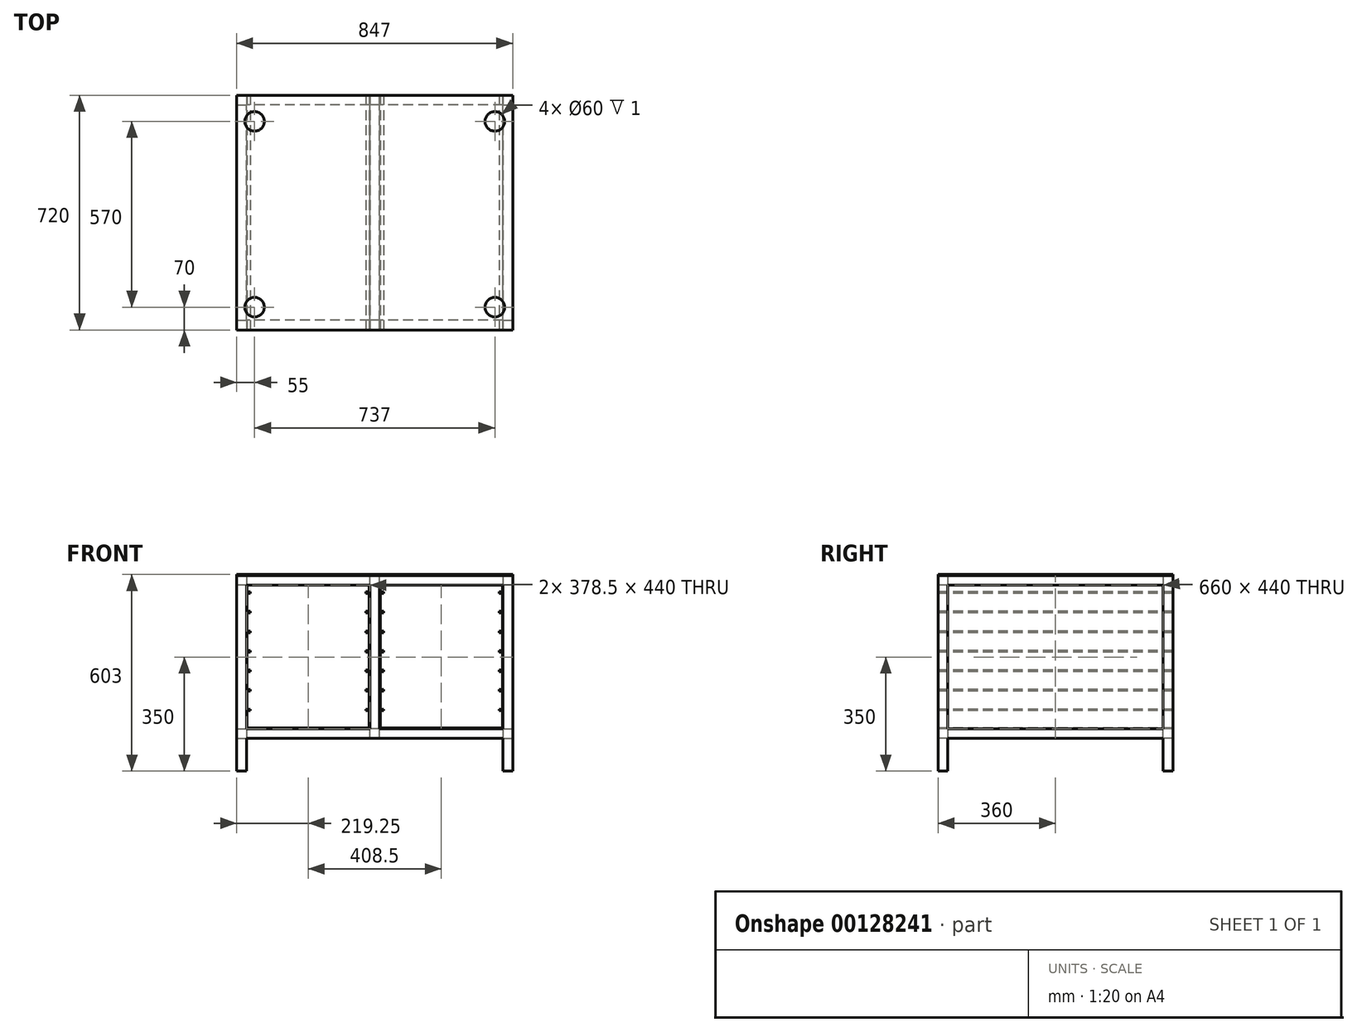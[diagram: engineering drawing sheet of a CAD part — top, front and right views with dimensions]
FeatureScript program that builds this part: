
annotation { "Feature Type Name" : "Feature", "Feature Type Description" : "" }
export const myFeature = defineFeature(function(context is Context, id is Id, definition is map)
    precondition{}
    {
        {
            var Q0;
            Q0=qCreatedBy(makeId("Top.planeOp"),FACE);
            var sketch = newSketch(context, id + "F0", { "sketchPlane" : qUnion([Q0])});
            skLineSegment(sketch, "E0.bottom", {"start": v(-423.5, 360) * mm, "end": v(-393.5, 360) * mm});
            skLineSegment(sketch, "E0.top", {"start": v(-423.5, 330) * mm, "end": v(-393.5, 330) * mm});
            skLineSegment(sketch, "E0.left", {"start": v(-423.5, 360) * mm, "end": v(-423.5, 330) * mm});
            skLineSegment(sketch, "E0.right", {"start": v(-393.5, 360) * mm, "end": v(-393.5, 330) * mm});
            skLineSegment(sketch, "E1.bottom", {"start": v(393.5, 360) * mm, "end": v(423.5, 360) * mm});
            skLineSegment(sketch, "E1.top", {"start": v(393.5, 330) * mm, "end": v(423.5, 330) * mm});
            skLineSegment(sketch, "E1.left", {"start": v(393.5, 360) * mm, "end": v(393.5, 330) * mm});
            skLineSegment(sketch, "E1.right", {"start": v(423.5, 360) * mm, "end": v(423.5, 330) * mm});
            skLineSegment(sketch, "E2.bottom", {"start": v(423.5, -330) * mm, "end": v(393.5, -330) * mm});
            skLineSegment(sketch, "E2.top", {"start": v(423.5, -360) * mm, "end": v(393.5, -360) * mm});
            skLineSegment(sketch, "E2.left", {"start": v(423.5, -330) * mm, "end": v(423.5, -360) * mm});
            skLineSegment(sketch, "E2.right", {"start": v(393.5, -330) * mm, "end": v(393.5, -360) * mm});
            skLineSegment(sketch, "E3.bottom", {"start": v(-423.5, -360) * mm, "end": v(-393.5, -360) * mm});
            skLineSegment(sketch, "E3.top", {"start": v(-423.5, -330) * mm, "end": v(-393.5, -330) * mm});
            skLineSegment(sketch, "E3.left", {"start": v(-423.5, -360) * mm, "end": v(-423.5, -330) * mm});
            skLineSegment(sketch, "E3.right", {"start": v(-393.5, -360) * mm, "end": v(-393.5, -330) * mm});
            skSolve(sketch);
        }
        {
            var Q0;
            Q0=makeQuery(id+"F0.imprint","IMPRINT",FACE,{"disambiguationData":[TD([[makeQuery(id+"F0.imprint","IMPRINT",EDGE,{"derivedFrom":sQuery(id+"F0.wireOp",EDGE,"E1.bottom")}),-1.0]])]});
            var Q1;
            Q1=makeQuery(id+"F0.imprint","IMPRINT",FACE,{"disambiguationData":[TD([[makeQuery(id+"F0.imprint","IMPRINT",EDGE,{"derivedFrom":sQuery(id+"F0.wireOp",EDGE,"E2.bottom")}),1.0]])]});
            var Q2;
            Q2=makeQuery(id+"F0.imprint","IMPRINT",FACE,{"disambiguationData":[TD([[makeQuery(id+"F0.imprint","IMPRINT",EDGE,{"derivedFrom":sQuery(id+"F0.wireOp",EDGE,"E0.bottom")}),-1.0]])]});
            var Q3;
            Q3=makeQuery(id+"F0.imprint","IMPRINT",FACE,{"disambiguationData":[TD([[makeQuery(id+"F0.imprint","IMPRINT",EDGE,{"derivedFrom":sQuery(id+"F0.wireOp",EDGE,"E3.bottom")}),1.0]])]});
            extrude(context, id + "F1", {"entities" : qUnion([Q0, Q1, Q2, Q3]), "depth" : 600 * mm});
        }
        {
            var Q0;
            Q0=qCreatedBy(makeId("Right.planeOp"),FACE);
            var sketch = newSketch(context, id + "F2", { "sketchPlane" : qUnion([Q0])});
            skLineSegment(sketch, "E4.bottom", {"start": v(360, 600) * mm, "end": v(330, 600) * mm});
            skLineSegment(sketch, "E4.top", {"start": v(360, 570) * mm, "end": v(330, 570) * mm});
            skLineSegment(sketch, "E4.left", {"start": v(360, 600) * mm, "end": v(360, 570) * mm});
            skLineSegment(sketch, "E4.right", {"start": v(330, 600) * mm, "end": v(330, 570) * mm});
            skLineSegment(sketch, "E5.bottom", {"start": v(-360, 600) * mm, "end": v(-330, 600) * mm});
            skLineSegment(sketch, "E5.top", {"start": v(-360, 570) * mm, "end": v(-330, 570) * mm});
            skLineSegment(sketch, "E5.left", {"start": v(-360, 600) * mm, "end": v(-360, 570) * mm});
            skLineSegment(sketch, "E5.right", {"start": v(-330, 600) * mm, "end": v(-330, 570) * mm});
            skLineSegment(sketch, "E6.bottom", {"start": v(360, 130) * mm, "end": v(330, 130) * mm});
            skLineSegment(sketch, "E6.top", {"start": v(360, 100) * mm, "end": v(330, 100) * mm});
            skLineSegment(sketch, "E6.left", {"start": v(360, 130) * mm, "end": v(360, 100) * mm});
            skLineSegment(sketch, "E6.right", {"start": v(330, 130) * mm, "end": v(330, 100) * mm});
            skLineSegment(sketch, "E7.bottom", {"start": v(-330, 130) * mm, "end": v(-360, 130) * mm});
            skLineSegment(sketch, "E7.top", {"start": v(-330, 100) * mm, "end": v(-360, 100) * mm});
            skLineSegment(sketch, "E7.left", {"start": v(-330, 130) * mm, "end": v(-330, 100) * mm});
            skLineSegment(sketch, "E7.right", {"start": v(-360, 130) * mm, "end": v(-360, 100) * mm});
            skSolve(sketch);
        }
        {
            var Q0;
            Q0 = qSketchRegion(id + "F2", true);
            extrude(context, id + "F3", {"entities" : qUnion([Q0]), "operationType" : NewBodyOperationType.ADD, "endBound" : BoundingType.UP_TO_NEXT, "depth" : 25 * mm, "hasSecondDirection" : true, "secondDirectionBound" : BoundingType.UP_TO_NEXT, "secondDirectionOppositeDirection" : true, "secondDirectionDepth" : 25 * mm});
        }
        {
            var Q0;
            Q0=qCreatedBy(makeId("Front.planeOp"),FACE);
            var sketch = newSketch(context, id + "F4", { "sketchPlane" : qUnion([Q0])});
            skLineSegment(sketch, "E8.bottom", {"start": v(423.5, 100) * mm, "end": v(393.5, 100) * mm});
            skLineSegment(sketch, "E8.top", {"start": v(423.5, 130) * mm, "end": v(393.5, 130) * mm});
            skLineSegment(sketch, "E8.left", {"start": v(423.5, 100) * mm, "end": v(423.5, 130) * mm});
            skLineSegment(sketch, "E8.right", {"start": v(393.5, 100) * mm, "end": v(393.5, 130) * mm});
            skPoint(sketch, "E9.oppositeSnap0", {"position": v(408.5, 130) * mm});
            skLineSegment(sketch, "E9.bottom", {"start": v(-393.5, 100) * mm, "end": v(-423.5, 100) * mm});
            skLineSegment(sketch, "E9.top", {"start": v(-393.5, 130) * mm, "end": v(-423.5, 130) * mm});
            skLineSegment(sketch, "E9.left", {"start": v(-393.5, 100) * mm, "end": v(-393.5, 130) * mm});
            skLineSegment(sketch, "E9.right", {"start": v(-423.5, 100) * mm, "end": v(-423.5, 130) * mm});
            skLineSegment(sketch, "E10.bottom", {"start": v(-423.5, 570) * mm, "end": v(-393.5, 570) * mm});
            skLineSegment(sketch, "E10.top", {"start": v(-423.5, 600) * mm, "end": v(-393.5, 600) * mm});
            skLineSegment(sketch, "E10.left", {"start": v(-423.5, 570) * mm, "end": v(-423.5, 600) * mm});
            skLineSegment(sketch, "E10.right", {"start": v(-393.5, 570) * mm, "end": v(-393.5, 600) * mm});
            skLineSegment(sketch, "E11.bottom", {"start": v(393.5, 570) * mm, "end": v(423.5, 570) * mm});
            skLineSegment(sketch, "E11.top", {"start": v(393.5, 600) * mm, "end": v(423.5, 600) * mm});
            skLineSegment(sketch, "E11.left", {"start": v(393.5, 570) * mm, "end": v(393.5, 600) * mm});
            skLineSegment(sketch, "E11.right", {"start": v(423.5, 570) * mm, "end": v(423.5, 600) * mm});
            skLineSegment(sketch, "E12.bottom", {"start": v(-15, 130) * mm, "end": v(15, 130) * mm});
            skLineSegment(sketch, "E12.top", {"start": v(-15, 100) * mm, "end": v(15, 100) * mm});
            skLineSegment(sketch, "E12.left", {"start": v(-15, 130) * mm, "end": v(-15, 100) * mm});
            skLineSegment(sketch, "E12.right", {"start": v(15, 130) * mm, "end": v(15, 100) * mm});
            skLineSegment(sketch, "E13.bottom", {"start": v(-15, 600) * mm, "end": v(15, 600) * mm});
            skLineSegment(sketch, "E13.top", {"start": v(-15, 570) * mm, "end": v(15, 570) * mm});
            skLineSegment(sketch, "E13.left", {"start": v(-15, 600) * mm, "end": v(-15, 570) * mm});
            skLineSegment(sketch, "E13.right", {"start": v(15, 600) * mm, "end": v(15, 570) * mm});
            skSolve(sketch);
        }
        {
            var Q0;
            Q0 = qSketchRegion(id + "F4", true);
            extrude(context, id + "F5", {"entities" : qUnion([Q0]), "operationType" : NewBodyOperationType.ADD, "endBound" : BoundingType.UP_TO_NEXT, "depth" : 25 * mm, "hasSecondDirection" : true, "secondDirectionBound" : BoundingType.UP_TO_NEXT, "secondDirectionOppositeDirection" : true, "secondDirectionDepth" : 25 * mm});
        }
        {
            var Q0;
            Q0=makeQuery(id+"F5.boolean.opBoolean","MERGE",FACE,{"derivedFrom":[makeQuery(id+"F3.boolean.opBoolean","MERGE",FACE,{"derivedFrom":[makeQuery(id+"F1.opExtrude","CAP_FACE",FACE,{"disambiguationData":[OSD([sQuery(id+"F0.wireOp",EDGE,"E0.bottom"),sQuery(id+"F0.wireOp",EDGE,"E0.top"),sQuery(id+"F0.wireOp",EDGE,"E0.left"),sQuery(id+"F0.wireOp",EDGE,"E0.right")])],"isStart":false}),makeQuery(id+"F1.opExtrude","CAP_FACE",FACE,{"disambiguationData":[OSD([sQuery(id+"F0.wireOp",EDGE,"E1.bottom"),sQuery(id+"F0.wireOp",EDGE,"E1.top"),sQuery(id+"F0.wireOp",EDGE,"E1.left"),sQuery(id+"F0.wireOp",EDGE,"E1.right")])],"isStart":false}),makeQuery(id+"F3.opExtrude","SWEPT_FACE",FACE,{"disambiguationData":[OSD([sQuery(id+"F2.wireOp",EDGE,"E4.bottom")])]})]}),makeQuery(id+"F3.boolean.opBoolean","MERGE",FACE,{"derivedFrom":[makeQuery(id+"F1.opExtrude","CAP_FACE",FACE,{"disambiguationData":[OSD([sQuery(id+"F0.wireOp",EDGE,"E2.bottom"),sQuery(id+"F0.wireOp",EDGE,"E2.top"),sQuery(id+"F0.wireOp",EDGE,"E2.left"),sQuery(id+"F0.wireOp",EDGE,"E2.right")])],"isStart":false}),makeQuery(id+"F1.opExtrude","CAP_FACE",FACE,{"disambiguationData":[OSD([sQuery(id+"F0.wireOp",EDGE,"E3.bottom"),sQuery(id+"F0.wireOp",EDGE,"E3.top"),sQuery(id+"F0.wireOp",EDGE,"E3.left"),sQuery(id+"F0.wireOp",EDGE,"E3.right")])],"isStart":false}),makeQuery(id+"F3.opExtrude","SWEPT_FACE",FACE,{"disambiguationData":[OSD([sQuery(id+"F2.wireOp",EDGE,"E5.bottom")])]})]}),makeQuery(id+"F5.opExtrude","SWEPT_FACE",FACE,{"disambiguationData":[OSD([sQuery(id+"F4.wireOp",EDGE,"E10.top")])]}),makeQuery(id+"F5.opExtrude","SWEPT_FACE",FACE,{"disambiguationData":[OSD([sQuery(id+"F4.wireOp",EDGE,"E11.top")])]})]});
            var sketch = newSketch(context, id + "F6", { "sketchPlane" : qUnion([Q0])});
            skLineSegment(sketch, "E14.bottom", {"start": v(-423.5, -360) * mm, "end": v(423.5, -360) * mm});
            skLineSegment(sketch, "E14.top", {"start": v(-423.5, 360) * mm, "end": v(423.5, 360) * mm});
            skLineSegment(sketch, "E14.left", {"start": v(-423.5, -360) * mm, "end": v(-423.5, 360) * mm});
            skLineSegment(sketch, "E14.right", {"start": v(423.5, -360) * mm, "end": v(423.5, 360) * mm});
            skSolve(sketch);
        }
        {
            var Q0;
            Q0 = qSketchRegion(id + "F6", true);
            extrude(context, id + "F7", {"entities" : qUnion([Q0]), "depth" : 3 * mm});
        }
        {
            var Q0;
            Q0=qCreatedBy(makeId("Top.planeOp"),FACE);
            cPlane(context, id + "F8", {"entities" : qUnion([Q0]), "cplaneType" : CPlaneType.OFFSET, "offset" : 300 * mm, "width" : 150 * mm, "height" : 150 * mm});
        }
        {
            var Q0;
            Q0=qCreatedBy(id+"F8.planeOp",FACE);
            var sketch = newSketch(context, id + "F9", { "sketchPlane" : qUnion([Q0])});
            skLineSegment(sketch, "E15.bottom", {"start": v(-15, 360) * mm, "end": v(15, 360) * mm});
            skLineSegment(sketch, "E15.top", {"start": v(-15, 330) * mm, "end": v(15, 330) * mm});
            skLineSegment(sketch, "E15.left", {"start": v(-15, 360) * mm, "end": v(-15, 330) * mm});
            skLineSegment(sketch, "E15.right", {"start": v(15, 360) * mm, "end": v(15, 330) * mm});
            skLineSegment(sketch, "E16.bottom", {"start": v(-15, -330) * mm, "end": v(15, -330) * mm});
            skLineSegment(sketch, "E16.top", {"start": v(-15, -360) * mm, "end": v(15, -360) * mm});
            skLineSegment(sketch, "E16.left", {"start": v(-15, -330) * mm, "end": v(-15, -360) * mm});
            skLineSegment(sketch, "E16.right", {"start": v(15, -330) * mm, "end": v(15, -360) * mm});
            skSolve(sketch);
        }
        {
            var Q0;
            Q0 = qSketchRegion(id + "F9", true);
            extrude(context, id + "F10", {"entities" : qUnion([Q0]), "operationType" : NewBodyOperationType.ADD, "endBound" : BoundingType.UP_TO_NEXT, "depth" : 25 * mm, "hasSecondDirection" : true, "secondDirectionBound" : BoundingType.UP_TO_NEXT, "secondDirectionOppositeDirection" : true, "secondDirectionDepth" : 25 * mm});
        }
        {
            var Q0;
            Q0=makeQuery(id+"F10.boolean.opBoolean","MERGE",FACE,{"derivedFrom":[makeQuery(id+"F3.boolean.opBoolean","MERGE",FACE,{"derivedFrom":[makeQuery(id+"F1.opExtrude","SWEPT_FACE",FACE,{"disambiguationData":[OSD([sQuery(id+"F0.wireOp",EDGE,"E2.top")])]}),makeQuery(id+"F1.opExtrude","SWEPT_FACE",FACE,{"disambiguationData":[OSD([sQuery(id+"F0.wireOp",EDGE,"E3.bottom")])]}),makeQuery(id+"F3.opExtrude","SWEPT_FACE",FACE,{"disambiguationData":[OSD([sQuery(id+"F2.wireOp",EDGE,"E5.left")])]}),makeQuery(id+"F3.opExtrude","SWEPT_FACE",FACE,{"disambiguationData":[OSD([sQuery(id+"F2.wireOp",EDGE,"E7.right")])]})]}),makeQuery(id+"F10.opExtrude","SWEPT_FACE",FACE,{"disambiguationData":[OSD([sQuery(id+"F9.wireOp",EDGE,"E16.top")])]})]});
            var sketch = newSketch(context, id + "F11", { "sketchPlane" : qUnion([Q0])});
            skLineSegment(sketch, "E17.bottom", {"start": v(-393.5, 570) * mm, "end": v(-391.5, 570) * mm});
            skLineSegment(sketch, "E17.top", {"start": v(-393.5, 130) * mm, "end": v(-391.5, 130) * mm});
            skLineSegment(sketch, "E17.left", {"start": v(-393.5, 570) * mm, "end": v(-393.5, 130) * mm});
            skLineSegment(sketch, "E17.right", {"start": v(-391.5, 570) * mm, "end": v(-391.5, 130) * mm});
            skLineSegment(sketch, "E18.bottom", {"start": v(-15, 570) * mm, "end": v(-17, 570) * mm});
            skLineSegment(sketch, "E18.top", {"start": v(-15, 130) * mm, "end": v(-17, 130) * mm});
            skLineSegment(sketch, "E18.left", {"start": v(-15, 570) * mm, "end": v(-15, 130) * mm});
            skLineSegment(sketch, "E18.right", {"start": v(-17, 570) * mm, "end": v(-17, 130) * mm});
            skLineSegment(sketch, "E19.bottom", {"start": v(15, 570) * mm, "end": v(17, 570) * mm});
            skLineSegment(sketch, "E19.top", {"start": v(15, 130) * mm, "end": v(17, 130) * mm});
            skLineSegment(sketch, "E19.left", {"start": v(15, 570) * mm, "end": v(15, 130) * mm});
            skLineSegment(sketch, "E19.right", {"start": v(17, 570) * mm, "end": v(17, 130) * mm});
            skLineSegment(sketch, "E20.bottom", {"start": v(393.5, 570) * mm, "end": v(391.5, 570) * mm});
            skLineSegment(sketch, "E20.top", {"start": v(393.5, 130) * mm, "end": v(391.5, 130) * mm});
            skLineSegment(sketch, "E20.left", {"start": v(393.5, 570) * mm, "end": v(393.5, 130) * mm});
            skLineSegment(sketch, "E20.right", {"start": v(391.5, 570) * mm, "end": v(391.5, 130) * mm});
            skLineSegment(sketch, "E21.bottom", {"start": v(-391.5, 130) * mm, "end": v(-17, 130) * mm});
            skLineSegment(sketch, "E21.top", {"start": v(-391.5, 132) * mm, "end": v(-17, 132) * mm});
            skLineSegment(sketch, "E21.left", {"start": v(-391.5, 130) * mm, "end": v(-391.5, 132) * mm});
            skLineSegment(sketch, "E21.right", {"start": v(-17, 130) * mm, "end": v(-17, 132) * mm});
            skLineSegment(sketch, "E22.bottom", {"start": v(17, 130) * mm, "end": v(391.5, 130) * mm});
            skLineSegment(sketch, "E22.top", {"start": v(17, 132) * mm, "end": v(391.5, 132) * mm});
            skLineSegment(sketch, "E22.left", {"start": v(17, 130) * mm, "end": v(17, 132) * mm});
            skLineSegment(sketch, "E22.right", {"start": v(391.5, 130) * mm, "end": v(391.5, 132) * mm});
            skSolve(sketch);
        }
        {
            var Q0;
            Q0 = qSketchRegion(id + "F11", true);
            extrude(context, id + "F12", {"entities" : qUnion([Q0]), "oppositeDirection" : true, "depth" : 720 * mm});
        }
        {
            var Q0;
            Q0=makeQuery(id+"F10.boolean.opBoolean","MERGE",FACE,{"derivedFrom":[makeQuery(id+"F3.boolean.opBoolean","MERGE",FACE,{"derivedFrom":[makeQuery(id+"F1.opExtrude","SWEPT_FACE",FACE,{"disambiguationData":[OSD([sQuery(id+"F0.wireOp",EDGE,"E2.top")])]}),makeQuery(id+"F1.opExtrude","SWEPT_FACE",FACE,{"disambiguationData":[OSD([sQuery(id+"F0.wireOp",EDGE,"E3.bottom")])]}),makeQuery(id+"F3.opExtrude","SWEPT_FACE",FACE,{"disambiguationData":[OSD([sQuery(id+"F2.wireOp",EDGE,"E5.left")])]}),makeQuery(id+"F3.opExtrude","SWEPT_FACE",FACE,{"disambiguationData":[OSD([sQuery(id+"F2.wireOp",EDGE,"E7.right")])]})]}),makeQuery(id+"F10.opExtrude","SWEPT_FACE",FACE,{"disambiguationData":[OSD([sQuery(id+"F9.wireOp",EDGE,"E16.top")])]})]});
            var sketch = newSketch(context, id + "F13", { "sketchPlane" : qUnion([Q0])});
            skLineSegment(sketch, "E23.bottom", {"start": v(-391.5, 550) * mm, "end": v(-381.5, 550) * mm});
            skLineSegment(sketch, "E23.top", {"start": v(-391.5, 545) * mm, "end": v(-381.5, 545) * mm});
            skLineSegment(sketch, "E23.left", {"start": v(-391.5, 550) * mm, "end": v(-391.5, 545) * mm});
            skLineSegment(sketch, "E23.right", {"start": v(-381.5, 550) * mm, "end": v(-381.5, 545) * mm});
            skLineSegment(sketch, "E24.0.1.0", {"start": v(-381.5, 490) * mm, "end": v(-381.5, 485) * mm});
            skLineSegment(sketch, "E24.0.1.1", {"start": v(-391.5, 490) * mm, "end": v(-391.5, 485) * mm});
            skLineSegment(sketch, "E24.0.1.2", {"start": v(-391.5, 485) * mm, "end": v(-381.5, 485) * mm});
            skLineSegment(sketch, "E24.0.1.3", {"start": v(-391.5, 490) * mm, "end": v(-381.5, 490) * mm});
            skLineSegment(sketch, "E24.0.2.0", {"start": v(-381.5, 430) * mm, "end": v(-381.5, 425) * mm});
            skLineSegment(sketch, "E24.0.2.1", {"start": v(-391.5, 430) * mm, "end": v(-391.5, 425) * mm});
            skLineSegment(sketch, "E24.0.2.2", {"start": v(-391.5, 425) * mm, "end": v(-381.5, 425) * mm});
            skLineSegment(sketch, "E24.0.2.3", {"start": v(-391.5, 430) * mm, "end": v(-381.5, 430) * mm});
            skLineSegment(sketch, "E24.0.3.0", {"start": v(-381.5, 370) * mm, "end": v(-381.5, 365) * mm});
            skLineSegment(sketch, "E24.0.3.1", {"start": v(-391.5, 370) * mm, "end": v(-391.5, 365) * mm});
            skLineSegment(sketch, "E24.0.3.2", {"start": v(-391.5, 365) * mm, "end": v(-381.5, 365) * mm});
            skLineSegment(sketch, "E24.0.3.3", {"start": v(-391.5, 370) * mm, "end": v(-381.5, 370) * mm});
            skLineSegment(sketch, "E24.0.4.0", {"start": v(-381.5, 310) * mm, "end": v(-381.5, 305) * mm});
            skLineSegment(sketch, "E24.0.4.1", {"start": v(-391.5, 310) * mm, "end": v(-391.5, 305) * mm});
            skLineSegment(sketch, "E24.0.4.2", {"start": v(-391.5, 305) * mm, "end": v(-381.5, 305) * mm});
            skLineSegment(sketch, "E24.0.4.3", {"start": v(-391.5, 310) * mm, "end": v(-381.5, 310) * mm});
            skLineSegment(sketch, "E24.0.5.0", {"start": v(-381.5, 250) * mm, "end": v(-381.5, 245) * mm});
            skLineSegment(sketch, "E24.0.5.1", {"start": v(-391.5, 250) * mm, "end": v(-391.5, 245) * mm});
            skLineSegment(sketch, "E24.0.5.2", {"start": v(-391.5, 245) * mm, "end": v(-381.5, 245) * mm});
            skLineSegment(sketch, "E24.0.5.3", {"start": v(-391.5, 250) * mm, "end": v(-381.5, 250) * mm});
            skLineSegment(sketch, "E24.0.6.0", {"start": v(-381.5, 190) * mm, "end": v(-381.5, 185) * mm});
            skLineSegment(sketch, "E24.0.6.1", {"start": v(-391.5, 190) * mm, "end": v(-391.5, 185) * mm});
            skLineSegment(sketch, "E24.0.6.2", {"start": v(-391.5, 185) * mm, "end": v(-381.5, 185) * mm});
            skLineSegment(sketch, "E24.0.6.3", {"start": v(-391.5, 190) * mm, "end": v(-381.5, 190) * mm});
            skLineSegment(sketch, "E24.1.0.0", {"start": v(-17, 550) * mm, "end": v(-17, 545) * mm});
            skLineSegment(sketch, "E24.1.0.1", {"start": v(-27, 550) * mm, "end": v(-27, 545) * mm});
            skLineSegment(sketch, "E24.1.0.2", {"start": v(-27, 545) * mm, "end": v(-17, 545) * mm});
            skLineSegment(sketch, "E24.1.0.3", {"start": v(-27, 550) * mm, "end": v(-17, 550) * mm});
            skLineSegment(sketch, "E24.1.1.0", {"start": v(-17, 490) * mm, "end": v(-17, 485) * mm});
            skLineSegment(sketch, "E24.1.1.1", {"start": v(-27, 490) * mm, "end": v(-27, 485) * mm});
            skLineSegment(sketch, "E24.1.1.2", {"start": v(-27, 485) * mm, "end": v(-17, 485) * mm});
            skLineSegment(sketch, "E24.1.1.3", {"start": v(-27, 490) * mm, "end": v(-17, 490) * mm});
            skLineSegment(sketch, "E24.1.2.0", {"start": v(-17, 430) * mm, "end": v(-17, 425) * mm});
            skLineSegment(sketch, "E24.1.2.1", {"start": v(-27, 430) * mm, "end": v(-27, 425) * mm});
            skLineSegment(sketch, "E24.1.2.2", {"start": v(-27, 425) * mm, "end": v(-17, 425) * mm});
            skLineSegment(sketch, "E24.1.2.3", {"start": v(-27, 430) * mm, "end": v(-17, 430) * mm});
            skLineSegment(sketch, "E24.1.3.0", {"start": v(-17, 370) * mm, "end": v(-17, 365) * mm});
            skLineSegment(sketch, "E24.1.3.1", {"start": v(-27, 370) * mm, "end": v(-27, 365) * mm});
            skLineSegment(sketch, "E24.1.3.2", {"start": v(-27, 365) * mm, "end": v(-17, 365) * mm});
            skLineSegment(sketch, "E24.1.3.3", {"start": v(-27, 370) * mm, "end": v(-17, 370) * mm});
            skLineSegment(sketch, "E24.1.4.0", {"start": v(-17, 310) * mm, "end": v(-17, 305) * mm});
            skLineSegment(sketch, "E24.1.4.1", {"start": v(-27, 310) * mm, "end": v(-27, 305) * mm});
            skLineSegment(sketch, "E24.1.4.2", {"start": v(-27, 305) * mm, "end": v(-17, 305) * mm});
            skLineSegment(sketch, "E24.1.4.3", {"start": v(-27, 310) * mm, "end": v(-17, 310) * mm});
            skLineSegment(sketch, "E24.1.5.0", {"start": v(-17, 250) * mm, "end": v(-17, 245) * mm});
            skLineSegment(sketch, "E24.1.5.1", {"start": v(-27, 250) * mm, "end": v(-27, 245) * mm});
            skLineSegment(sketch, "E24.1.5.2", {"start": v(-27, 245) * mm, "end": v(-17, 245) * mm});
            skLineSegment(sketch, "E24.1.5.3", {"start": v(-27, 250) * mm, "end": v(-17, 250) * mm});
            skLineSegment(sketch, "E24.1.6.0", {"start": v(-17, 190) * mm, "end": v(-17, 185) * mm});
            skLineSegment(sketch, "E24.1.6.1", {"start": v(-27, 190) * mm, "end": v(-27, 185) * mm});
            skLineSegment(sketch, "E24.1.6.2", {"start": v(-27, 185) * mm, "end": v(-17, 185) * mm});
            skLineSegment(sketch, "E24.1.6.3", {"start": v(-27, 190) * mm, "end": v(-17, 190) * mm});
            skLineSegment(sketch, "E24.direction1", {"start": v(-391.5, 545) * mm, "end": v(-27, 545) * mm, "construction": true});
            skLineSegment(sketch, "E24.direction2", {"start": v(-391.5, 545) * mm, "end": v(-391.5, 485) * mm, "construction": true});
            skLineSegment(sketch, "E25.MirrorCS", {"start": v(391.5, 190) * mm, "end": v(381.5, 190) * mm});
            skLineSegment(sketch, "E26.MirrorCS", {"start": v(381.5, 190) * mm, "end": v(381.5, 185) * mm});
            skLineSegment(sketch, "E27.MirrorCS", {"start": v(391.5, 185) * mm, "end": v(381.5, 185) * mm});
            skLineSegment(sketch, "E28.MirrorCS", {"start": v(27, 550) * mm, "end": v(27, 545) * mm});
            skLineSegment(sketch, "E29.MirrorCS", {"start": v(391.5, 550) * mm, "end": v(381.5, 550) * mm});
            skLineSegment(sketch, "E30.MirrorCS", {"start": v(391.5, 545) * mm, "end": v(381.5, 545) * mm});
            skLineSegment(sketch, "E31.MirrorCS", {"start": v(391.5, 550) * mm, "end": v(391.5, 545) * mm});
            skLineSegment(sketch, "E32.MirrorCS", {"start": v(27, 550) * mm, "end": v(17, 550) * mm});
            skLineSegment(sketch, "E33.MirrorCS", {"start": v(27, 185) * mm, "end": v(17, 185) * mm});
            skLineSegment(sketch, "E34.MirrorCS", {"start": v(17, 550) * mm, "end": v(17, 545) * mm});
            skLineSegment(sketch, "E35.MirrorCS", {"start": v(27, 545) * mm, "end": v(17, 545) * mm});
            skLineSegment(sketch, "E36.MirrorCS", {"start": v(27, 190) * mm, "end": v(27, 185) * mm});
            skLineSegment(sketch, "E37.MirrorCS", {"start": v(391.5, 490) * mm, "end": v(381.5, 490) * mm});
            skLineSegment(sketch, "E38.MirrorCS", {"start": v(391.5, 485) * mm, "end": v(381.5, 485) * mm});
            skLineSegment(sketch, "E39.MirrorCS", {"start": v(391.5, 490) * mm, "end": v(391.5, 485) * mm});
            skLineSegment(sketch, "E40.MirrorCS", {"start": v(27, 190) * mm, "end": v(17, 190) * mm});
            skLineSegment(sketch, "E41.MirrorCS", {"start": v(27, 490) * mm, "end": v(27, 485) * mm});
            skLineSegment(sketch, "E42.MirrorCS", {"start": v(27, 250) * mm, "end": v(27, 245) * mm});
            skLineSegment(sketch, "E43.MirrorCS", {"start": v(17, 370) * mm, "end": v(17, 365) * mm});
            skLineSegment(sketch, "E44.MirrorCS", {"start": v(27, 370) * mm, "end": v(27, 365) * mm});
            skLineSegment(sketch, "E45.MirrorCS", {"start": v(391.5, 190) * mm, "end": v(391.5, 185) * mm});
            skLineSegment(sketch, "E46.MirrorCS", {"start": v(27, 310) * mm, "end": v(27, 305) * mm});
            skLineSegment(sketch, "E47.MirrorCS", {"start": v(17, 190) * mm, "end": v(17, 185) * mm});
            skLineSegment(sketch, "E48.MirrorCS", {"start": v(17, 490) * mm, "end": v(17, 485) * mm});
            skLineSegment(sketch, "E49.MirrorCS", {"start": v(17, 250) * mm, "end": v(17, 245) * mm});
            skLineSegment(sketch, "E50.MirrorCS", {"start": v(381.5, 310) * mm, "end": v(381.5, 305) * mm});
            skLineSegment(sketch, "E51.MirrorCS", {"start": v(391.5, 245) * mm, "end": v(381.5, 245) * mm});
            skLineSegment(sketch, "E52.MirrorCS", {"start": v(27, 425) * mm, "end": v(17, 425) * mm});
            skLineSegment(sketch, "E53.MirrorCS", {"start": v(27, 310) * mm, "end": v(17, 310) * mm});
            skLineSegment(sketch, "E54.MirrorCS", {"start": v(17, 310) * mm, "end": v(17, 305) * mm});
            skLineSegment(sketch, "E55.MirrorCS", {"start": v(27, 430) * mm, "end": v(27, 425) * mm});
            skLineSegment(sketch, "E56.MirrorCS", {"start": v(27, 305) * mm, "end": v(17, 305) * mm});
            skLineSegment(sketch, "E57.MirrorCS", {"start": v(391.5, 250) * mm, "end": v(391.5, 245) * mm});
            skLineSegment(sketch, "E58.MirrorCS", {"start": v(27, 370) * mm, "end": v(17, 370) * mm});
            skLineSegment(sketch, "E59.MirrorCS", {"start": v(381.5, 370) * mm, "end": v(381.5, 365) * mm});
            skLineSegment(sketch, "E60.MirrorCS", {"start": v(391.5, 430) * mm, "end": v(381.5, 430) * mm});
            skLineSegment(sketch, "E61.MirrorCS", {"start": v(391.5, 425) * mm, "end": v(381.5, 425) * mm});
            skLineSegment(sketch, "E62.MirrorCS", {"start": v(391.5, 430) * mm, "end": v(391.5, 425) * mm});
            skLineSegment(sketch, "E63.MirrorCS", {"start": v(381.5, 430) * mm, "end": v(381.5, 425) * mm});
            skLineSegment(sketch, "E64.MirrorCS", {"start": v(391.5, 310) * mm, "end": v(391.5, 305) * mm});
            skLineSegment(sketch, "E65.MirrorCS", {"start": v(391.5, 250) * mm, "end": v(381.5, 250) * mm});
            skLineSegment(sketch, "E66.MirrorCS", {"start": v(27, 430) * mm, "end": v(17, 430) * mm});
            skLineSegment(sketch, "E67.MirrorCS", {"start": v(391.5, 305) * mm, "end": v(381.5, 305) * mm});
            skLineSegment(sketch, "E68.MirrorCS", {"start": v(27, 245) * mm, "end": v(17, 245) * mm});
            skLineSegment(sketch, "E69.MirrorCS", {"start": v(27, 485) * mm, "end": v(17, 485) * mm});
            skLineSegment(sketch, "E70.MirrorCS", {"start": v(391.5, 310) * mm, "end": v(381.5, 310) * mm});
            skLineSegment(sketch, "E71.MirrorCS", {"start": v(27, 250) * mm, "end": v(17, 250) * mm});
            skLineSegment(sketch, "E72.MirrorCS", {"start": v(27, 490) * mm, "end": v(17, 490) * mm});
            skLineSegment(sketch, "E73.MirrorCS", {"start": v(27, 365) * mm, "end": v(17, 365) * mm});
            skLineSegment(sketch, "E74.MirrorCS", {"start": v(381.5, 250) * mm, "end": v(381.5, 245) * mm});
            skLineSegment(sketch, "E75.MirrorCS", {"start": v(17, 430) * mm, "end": v(17, 425) * mm});
            skLineSegment(sketch, "E76.MirrorCS", {"start": v(391.5, 370) * mm, "end": v(391.5, 365) * mm});
            skLineSegment(sketch, "E77.MirrorCS", {"start": v(391.5, 365) * mm, "end": v(381.5, 365) * mm});
            skLineSegment(sketch, "E78.MirrorCS", {"start": v(391.5, 370) * mm, "end": v(381.5, 370) * mm});
            skLineSegment(sketch, "E79.MirrorCS", {"start": v(381.5, 550) * mm, "end": v(381.5, 545) * mm});
            skLineSegment(sketch, "E80.MirrorCS", {"start": v(381.5, 490) * mm, "end": v(381.5, 485) * mm});
            skLineSegment(sketch, "E81.MirrorCS", {"start": v(391.5, 545) * mm, "end": v(27, 545) * mm, "construction": true});
            skLineSegment(sketch, "E82.MirrorCS", {"start": v(391.5, 545) * mm, "end": v(391.5, 485) * mm, "construction": true});
            skSolve(sketch);
        }
        {
            var Q0;
            Q0 = qSketchRegion(id + "F13", true);
            extrude(context, id + "F14", {"entities" : qUnion([Q0]), "operationType" : NewBodyOperationType.ADD, "oppositeDirection" : true, "depth" : 720 * mm});
        }
        {
            var Q0;
            Q0=makeQuery(id+"F7.opExtrude","CAP_FACE",FACE,{"disambiguationData":[OSD([sQuery(id+"F6.wireOp",EDGE,"E14.bottom"),sQuery(id+"F6.wireOp",EDGE,"E14.top"),sQuery(id+"F6.wireOp",EDGE,"E14.left"),sQuery(id+"F6.wireOp",EDGE,"E14.right")])],"isStart":false});
            var sketch = newSketch(context, id + "F15", { "sketchPlane" : qUnion([Q0])});
            skCircle(sketch, "E83", {"center": v(-368.5, 280) * mm, "radius": 30 * mm});
            skCircle(sketch, "E84", {"center": v(368.5, 280) * mm, "radius": 30 * mm});
            skCircle(sketch, "E85", {"center": v(368.5, -290) * mm, "radius": 30 * mm});
            skCircle(sketch, "E86", {"center": v(-368.5, -290) * mm, "radius": 30 * mm});
            skSolve(sketch);
        }
        {
            var Q0;
            Q0 = qSketchRegion(id + "F15", true);
            extrude(context, id + "F16", {"entities" : qUnion([Q0]), "operationType" : NewBodyOperationType.REMOVE, "oppositeDirection" : true, "depth" : 1 * mm});
        }
    });
